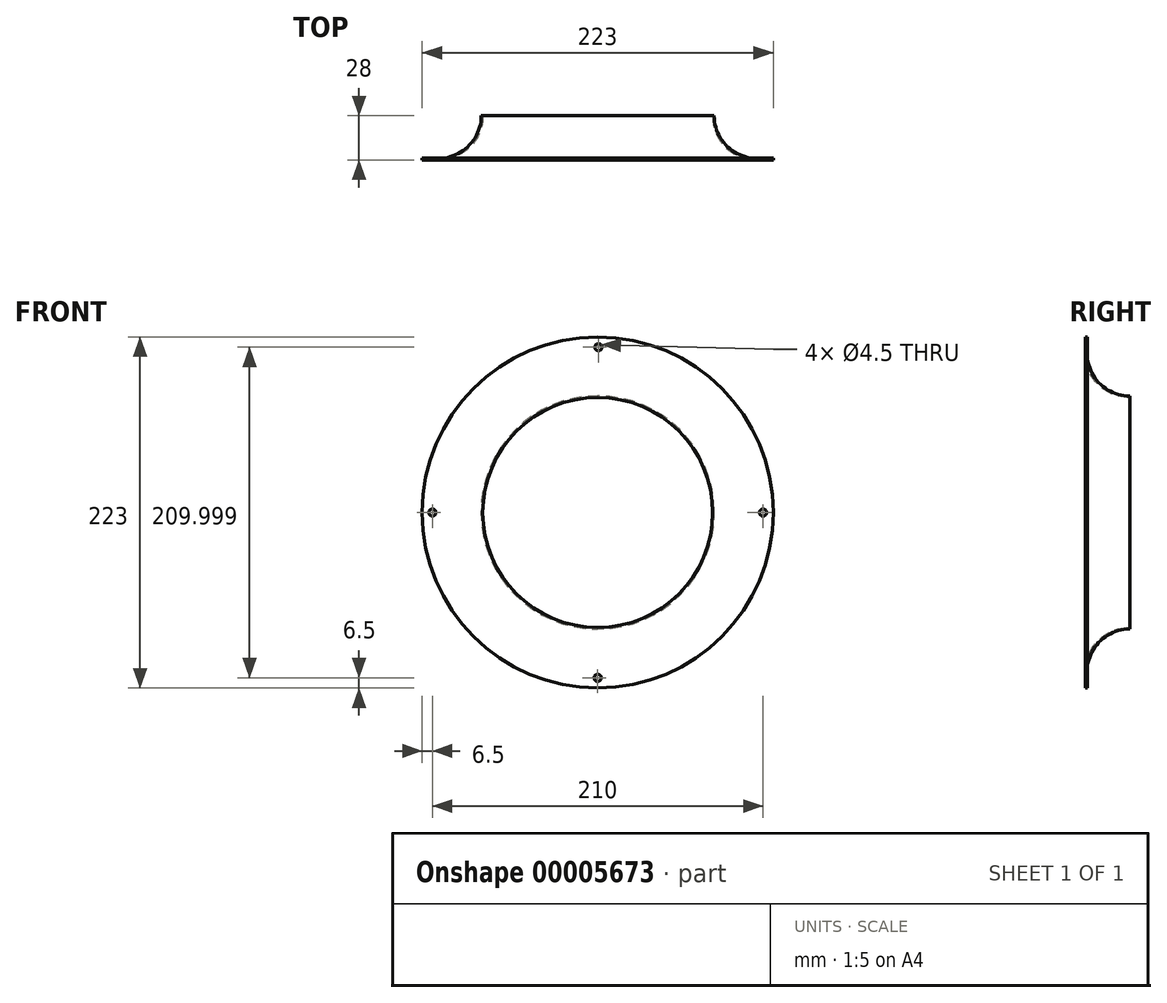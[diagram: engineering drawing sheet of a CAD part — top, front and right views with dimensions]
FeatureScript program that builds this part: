
annotation { "Feature Type Name" : "Feature", "Feature Type Description" : "" }
export const myFeature = defineFeature(function(context is Context, id is Id, definition is map)
    precondition{}
    {
        {
            var Q0;
            Q0=qCreatedBy(makeId("Right.planeOp"),FACE);
            var sketch = newSketch(context, id + "F0", { "sketchPlane" : qUnion([Q0])});
            skLineSegment(sketch, "E0", {"start": v(121.02, 73) * mm, "end": v(-120.73, 73) * mm, "construction": true});
            skLineSegment(sketch, "E1", {"start": v(-120.73, 73) * mm, "end": v(-120.73, 111.5) * mm, "construction": true});
            skLineSegment(sketch, "E2", {"start": v(-120.73, 111.5) * mm, "end": v(121.12, 111.5) * mm, "construction": true});
            skLineSegment(sketch, "E3", {"start": v(121.02, 73) * mm, "end": v(121.02, 0) * mm, "construction": true});
            skLineSegment(sketch, "E4", {"start": v(0, 0) * mm, "end": v(0, 139.41) * mm, "construction": true});
            skLineSegment(sketch, "E5", {"start": v(28, 0) * mm, "end": v(28, 141.5) * mm, "construction": true});
            skLineSegment(sketch, "E6", {"start": v(0, 0) * mm, "end": v(28, 0) * mm, "construction": true});
            skLineSegment(sketch, "E7", {"start": v(-48.91, 73) * mm, "end": v(-48.91, 101) * mm, "construction": true});
            skLineSegment(sketch, "E8", {"start": v(-48.91, 101) * mm, "end": v(57.82, 101) * mm, "construction": true});
            skArc(sketch, "E9", {"start": v(0, 101) * mm, "mid": v(8.2, 81.2) * mm, "end": v(28, 73) * mm});
            skLineSegment(sketch, "E10", {"start": v(0, 111.5) * mm, "end": v(0, 101) * mm});
            skArc(sketch, "E11.0", {"start": v(1, 101) * mm, "mid": v(8.9, 81.9) * mm, "end": v(28, 74) * mm});
            skLineSegment(sketch, "E11.1", {"start": v(1, 111.5) * mm, "end": v(1, 101) * mm});
            skLineSegment(sketch, "E12", {"start": v(28, 73) * mm, "end": v(28, 74) * mm});
            skLineSegment(sketch, "E13", {"start": v(1, 111.5) * mm, "end": v(0, 111.5) * mm});
            skCircle(sketch, "E14", {"center": v(-105, 0) * mm, "radius": 2.25 * mm});
            skSolve(sketch);
        }
        {
            var Q0;
            Q0=makeQuery(id+"F0.imprint","IMPRINT",FACE,{"disambiguationData":[TD([[makeQuery(id+"F0.imprint","IMPRINT",EDGE,{"derivedFrom":sQuery(id+"F0.wireOp",EDGE,"E9")}),1.0]])]});
            var Q1;
            Q1=sQuery(id+"F0.wireOp",EDGE,"E6");
            revolve(context, id + "F1", {"entities" : qUnion([Q0]), "axis" : qUnion([Q1]), "revolveType" : RevolveType.FULL});
        }
        {
            var Q0;
            Q0=qCreatedBy(makeId("Front.planeOp"),FACE);
            var sketch = newSketch(context, id + "F2", { "sketchPlane" : qUnion([Q0])});
            skCircle(sketch, "E15", {"center": v(0, 0) * mm, "radius": 105 * mm, "construction": true});
            skLineSegment(sketch, "E16", {"start": v(0, 0) * mm, "end": v(-138.38, 0) * mm, "construction": true});
            skLineSegment(sketch, "E17", {"start": v(0, 0) * mm, "end": v(127.61, 0) * mm, "construction": true});
            skLineSegment(sketch, "E18", {"start": v(0, 0) * mm, "end": v(0, -121.96) * mm, "construction": true});
            skCircle(sketch, "E19", {"center": v(0, -105) * mm, "radius": 2.25 * mm});
            skCircle(sketch, "E20", {"center": v(105, 0) * mm, "radius": 2.25 * mm});
            skCircle(sketch, "E21", {"center": v(-105, 0) * mm, "radius": 2.25 * mm});
            skLineSegment(sketch, "E22", {"start": v(0, 0) * mm, "end": v(0.64, 134.64) * mm, "construction": true});
            skCircle(sketch, "E23", {"center": v(0.5, 105) * mm, "radius": 2.25 * mm});
            skSolve(sketch);
        }
        {
            var Q0;
            Q0=makeQuery(id+"F2.imprint","IMPRINT",FACE,{"disambiguationData":[TD([[makeQuery(id+"F2.imprint","IMPRINT",EDGE,{"derivedFrom":sQuery(id+"F2.wireOp",EDGE,"E23")}),1.0]])]});
            var Q1;
            Q1=makeQuery(id+"F2.imprint","IMPRINT",FACE,{"disambiguationData":[TD([[makeQuery(id+"F2.imprint","IMPRINT",EDGE,{"derivedFrom":sQuery(id+"F2.wireOp",EDGE,"E21")}),1.0]])]});
            var Q2;
            Q2=makeQuery(id+"F2.imprint","IMPRINT",FACE,{"disambiguationData":[TD([[makeQuery(id+"F2.imprint","IMPRINT",EDGE,{"derivedFrom":sQuery(id+"F2.wireOp",EDGE,"E19")}),1.0]])]});
            var Q3;
            Q3=makeQuery(id+"F2.imprint","IMPRINT",FACE,{"disambiguationData":[TD([[makeQuery(id+"F2.imprint","IMPRINT",EDGE,{"derivedFrom":sQuery(id+"F2.wireOp",EDGE,"E20")}),1.0]])]});
            var Q4;
            Q4=sQuery(id+"F2.wireOp",EDGE,"E23");
            var Q5;
            Q5=sQuery(id+"F2.wireOp",EDGE,"E21");
            var Q6;
            Q6=sQuery(id+"F2.wireOp",EDGE,"E19");
            var Q7;
            Q7=sQuery(id+"F2.wireOp",EDGE,"E20");
            var Q8;
            Q8=makeQuery(id+"F1.opRevolve","SWEPT_FACE",FACE,{"disambiguationData":[OSD([sQuery(id+"F0.wireOp",EDGE,"E11.1")])]});
            extrude(context, id + "F3", {"entities" : qUnion([Q0, Q1, Q2, Q3]), "operationType" : NewBodyOperationType.REMOVE, "surfaceEntities" : qUnion([Q4, Q5, Q6, Q7]), "oppositeDirection" : true, "endBoundEntity" : qUnion([Q8]), "depth" : 3 * mm});
        }
    });
